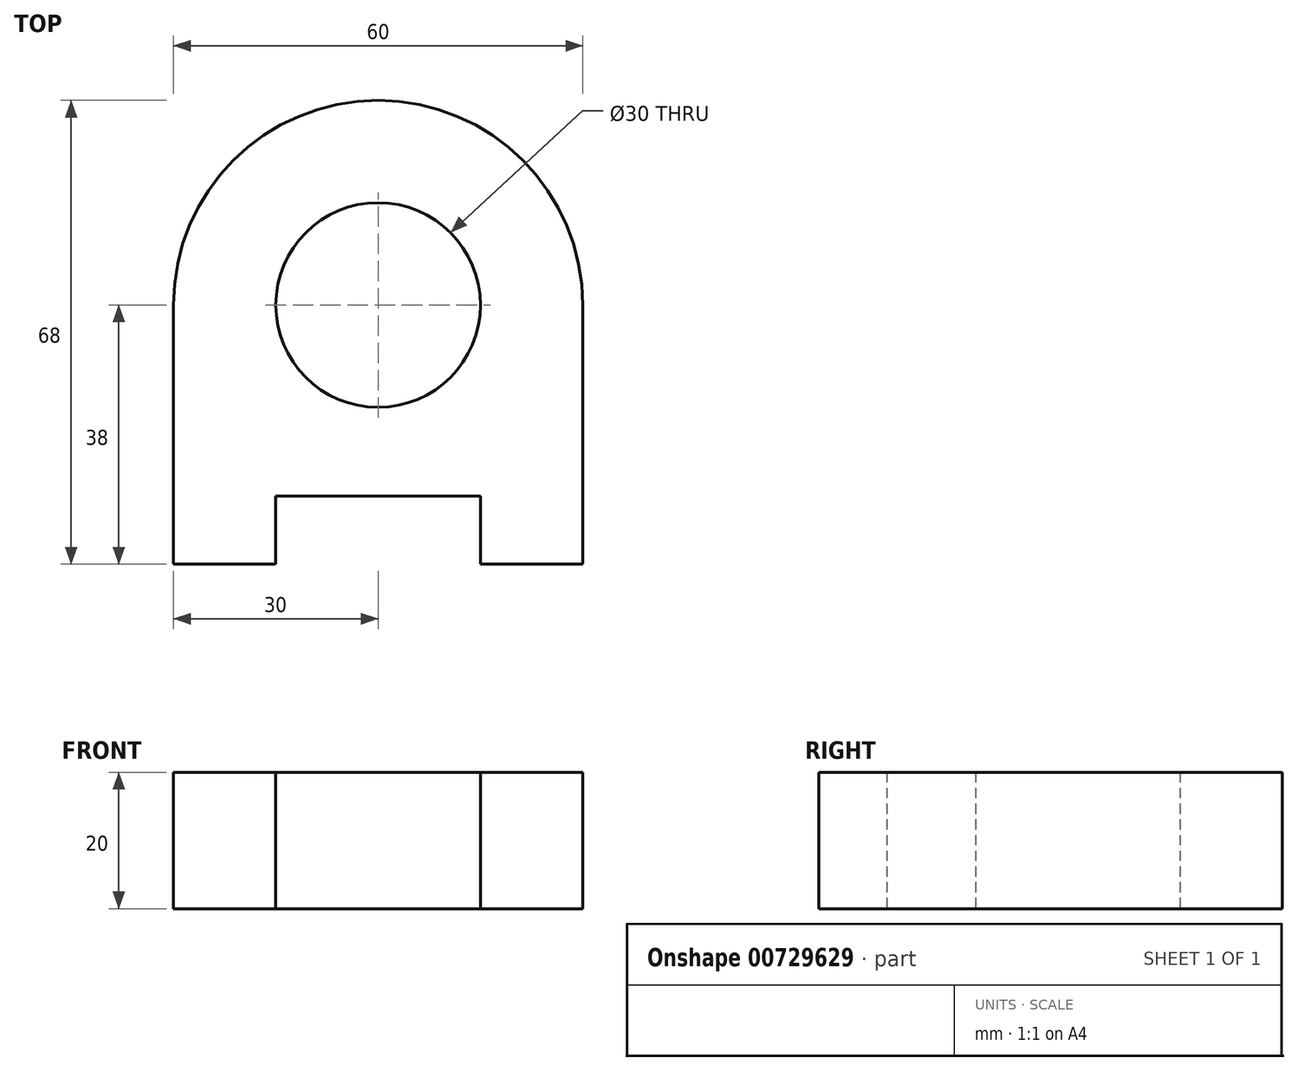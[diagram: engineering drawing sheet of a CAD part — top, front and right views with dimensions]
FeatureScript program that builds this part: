
annotation { "Feature Type Name" : "Feature", "Feature Type Description" : "" }
export const myFeature = defineFeature(function(context is Context, id is Id, definition is map)
    precondition{}
    {
        {
            var Q0;
            Q0=qCreatedBy(makeId("Top.planeOp"),FACE);
            var sketch = newSketch(context, id + "F0", { "sketchPlane" : qUnion([Q0])});
            skCircle(sketch, "E0", {"center": v(0, 0) * mm, "radius": 15 * mm});
            skArc(sketch, "E1", {"start": v(-30, 0) * mm, "mid": v(0, 30) * mm, "end": v(30, 0) * mm});
            skLineSegment(sketch, "E2", {"start": v(-30, 0) * mm, "end": v(-30, -38) * mm});
            skLineSegment(sketch, "E3", {"start": v(-30, -38) * mm, "end": v(-15, -38) * mm});
            skLineSegment(sketch, "E4", {"start": v(-15, -28) * mm, "end": v(15, -28) * mm});
            skLineSegment(sketch, "E5", {"start": v(15, -28) * mm, "end": v(15, -38) * mm});
            skLineSegment(sketch, "E6", {"start": v(15, -38) * mm, "end": v(30, -38) * mm});
            skLineSegment(sketch, "E7", {"start": v(-15, -28) * mm, "end": v(-15, -38) * mm});
            skLineSegment(sketch, "E8", {"start": v(30, -38) * mm, "end": v(30, 0) * mm});
            skSolve(sketch);
        }
        {
            var Q0;
            Q0 = qSketchRegion(id + "F0", true);
            extrude(context, id + "F1", {"entities" : qUnion([Q0]), "depth" : 20 * mm, "offsetDistance" : 25 * mm});
        }
    });
